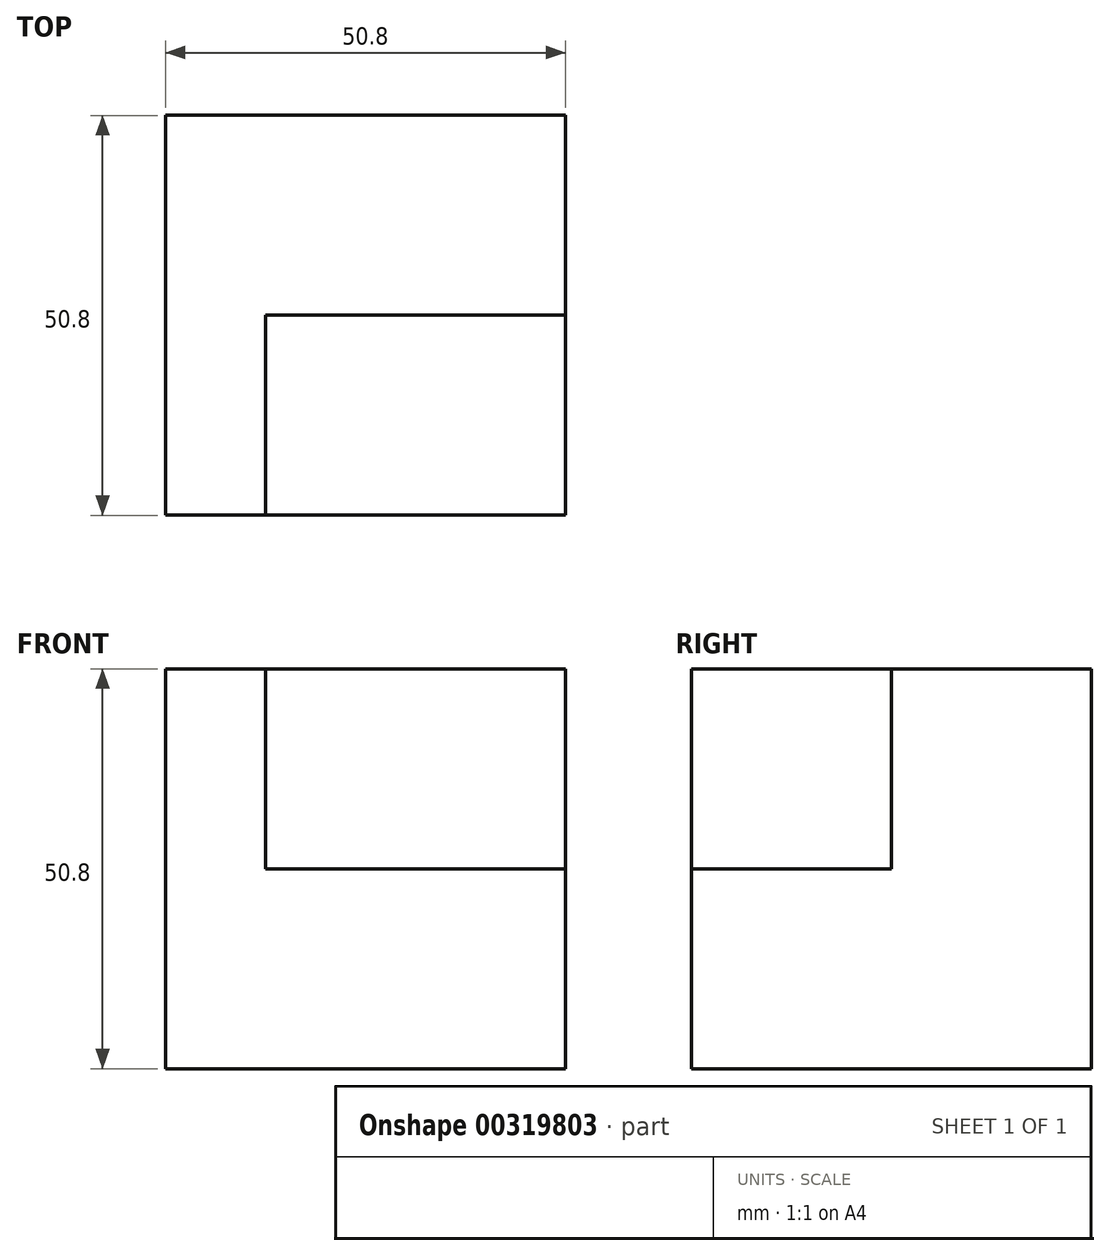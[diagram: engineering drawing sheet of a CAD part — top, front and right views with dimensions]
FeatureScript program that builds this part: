
annotation { "Feature Type Name" : "Feature", "Feature Type Description" : "" }
export const myFeature = defineFeature(function(context is Context, id is Id, definition is map)
    precondition{}
    {
        {
            var Q0;
            Q0=qCreatedBy(makeId("Top.planeOp"),FACE);
            var sketch = newSketch(context, id + "F0", { "sketchPlane" : qUnion([Q0])});
            skLineSegment(sketch, "E0", {"start": v(-19.13, -10.17) * mm, "end": v(31.67, -10.17) * mm});
            skLineSegment(sketch, "E1", {"start": v(31.67, -10.17) * mm, "end": v(31.67, 40.63) * mm});
            skLineSegment(sketch, "E2", {"start": v(31.67, 40.63) * mm, "end": v(-19.13, 40.63) * mm});
            skLineSegment(sketch, "E3", {"start": v(-19.13, 40.63) * mm, "end": v(-19.13, -10.17) * mm});
            skSolve(sketch);
        }
        {
            var Q0;
            Q0=makeQuery(id+"F0.imprint","IMPRINT",FACE,{"disambiguationData":[TD([[makeQuery(id+"F0.imprint","IMPRINT",EDGE,{"derivedFrom":sQuery(id+"F0.wireOp",EDGE,"E0")}),1.0]])]});
            extrude(context, id + "F1", {"entities" : qUnion([Q0]), "depth" : 50.8 * mm});
        }
        {
            var Q0;
            Q0=makeQuery(id+"F1.opExtrude","SWEPT_FACE",FACE,{"disambiguationData":[OSD([sQuery(id+"F0.wireOp",EDGE,"E0")])]});
            var sketch = newSketch(context, id + "F2", { "sketchPlane" : qUnion([Q0])});
            skLineSegment(sketch, "E4", {"start": v(31.67, 25.4) * mm, "end": v(-6.43, 25.4) * mm});
            skLineSegment(sketch, "E5", {"start": v(-6.43, 25.4) * mm, "end": v(-6.43, 50.8) * mm});
            skLineSegment(sketch, "E6", {"start": v(31.67, 50.8) * mm, "end": v(-6.43, 50.8) * mm});
            skLineSegment(sketch, "E7", {"start": v(31.67, 25.4) * mm, "end": v(31.67, 50.8) * mm});
            skLineSegment(sketch, "E8", {"start": v(-6.43, 50.8) * mm, "end": v(31.67, 50.8) * mm});
            skSolve(sketch);
        }
        {
            var Q0;
            Q0=makeQuery(id+"F2.imprint","IMPRINT",FACE,{"disambiguationData":[TD([[makeQuery(id+"F2.imprint","IMPRINT",EDGE,{"derivedFrom":sQuery(id+"F2.wireOp",EDGE,"E4")}),-1.0]])]});
            extrude(context, id + "F3", {"entities" : qUnion([Q0]), "operationType" : NewBodyOperationType.REMOVE, "oppositeDirection" : true, "depth" : 25.4 * mm});
        }
    });
